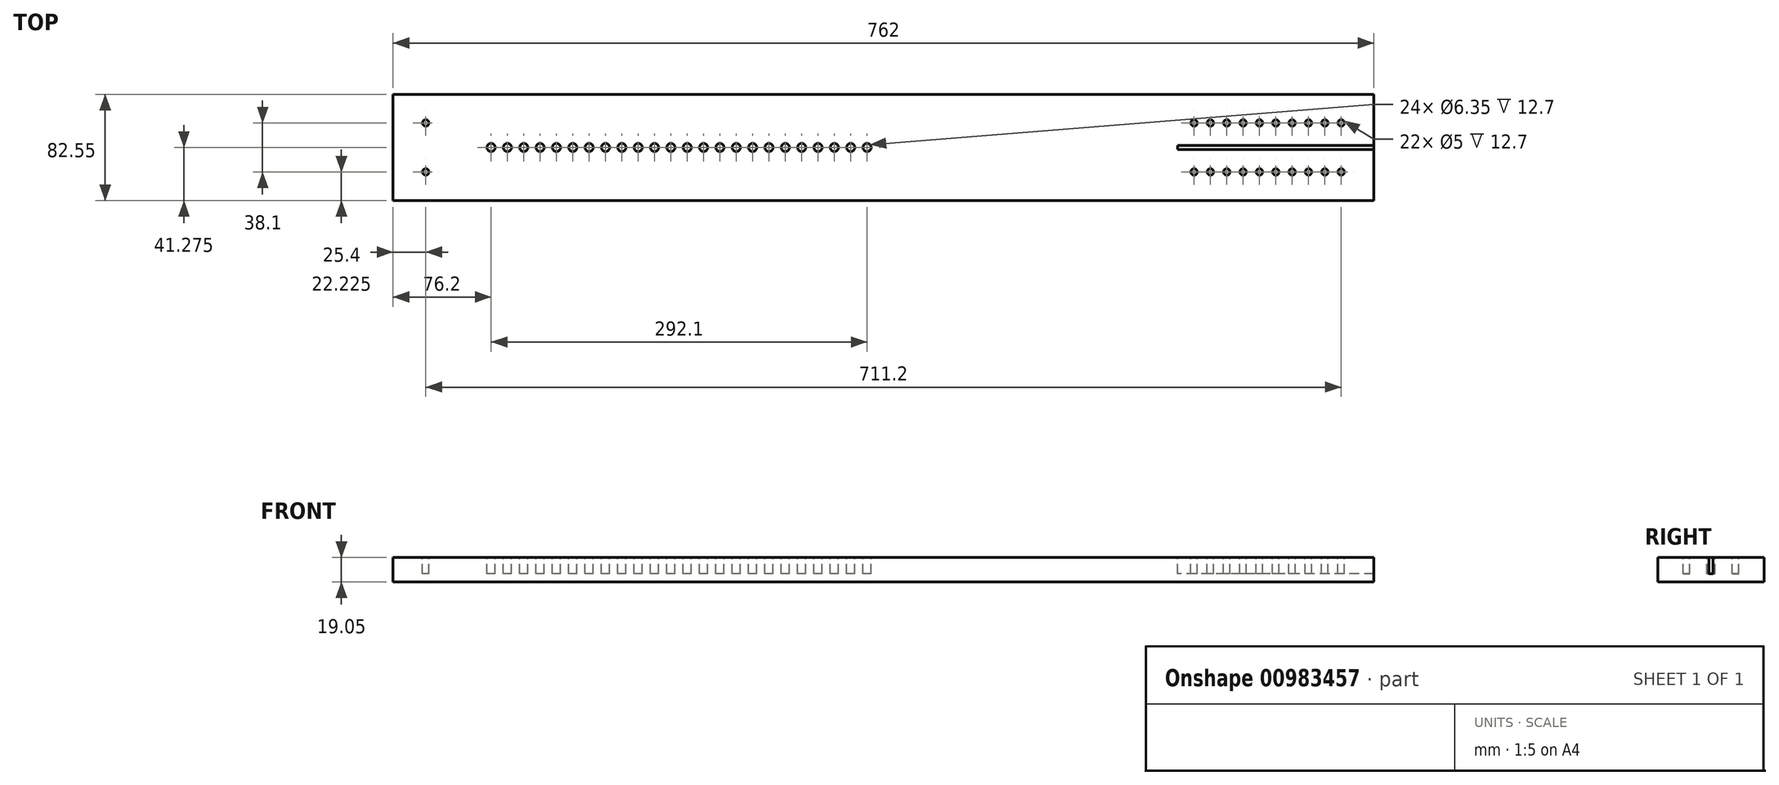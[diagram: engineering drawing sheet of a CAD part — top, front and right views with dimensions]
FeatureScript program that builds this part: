
annotation { "Feature Type Name" : "Feature", "Feature Type Description" : "" }
export const myFeature = defineFeature(function(context is Context, id is Id, definition is map)
    precondition{}
    {
        {
            var Q0;
            Q0=qCreatedBy(makeId("Top.planeOp"),FACE);
            var sketch = newSketch(context, id + "F0", { "sketchPlane" : qUnion([Q0])});
            skLineSegment(sketch, "E0.bottom", {"start": v(0, 0) * mm, "end": v(762, 0) * mm});
            skLineSegment(sketch, "E0.top", {"start": v(0, -82.55) * mm, "end": v(762, -82.55) * mm});
            skLineSegment(sketch, "E0.left", {"start": v(0, 0) * mm, "end": v(0, -82.55) * mm});
            skLineSegment(sketch, "E0.right", {"start": v(762, 0) * mm, "end": v(762, -82.55) * mm});
            skSolve(sketch);
        }
        {
            var Q0;
            Q0 = qSketchRegion(id + "F0", true);
            extrude(context, id + "F1", {"entities" : qUnion([Q0]), "depth" : 19.05 * mm, "offsetDistance" : 25.4 * mm});
        }
        {
            var Q0;
            Q0=makeQuery(id+"F1.opExtrude","CAP_FACE",FACE,{"disambiguationData":[OSD([sQuery(id+"F0.wireOp",EDGE,"E0.bottom"),sQuery(id+"F0.wireOp",EDGE,"E0.top"),sQuery(id+"F0.wireOp",EDGE,"E0.left"),sQuery(id+"F0.wireOp",EDGE,"E0.right")])],"isStart":false});
            var sketch = newSketch(context, id + "F2", { "sketchPlane" : qUnion([Q0])});
            skCircle(sketch, "E1", {"center": v(25.4, -22.23) * mm, "radius": 2.5 * mm});
            skCircle(sketch, "E2", {"center": v(25.4, -60.33) * mm, "radius": 2.5 * mm});
            skCircle(sketch, "E3", {"center": v(76.2, -41.28) * mm, "radius": 3.18 * mm});
            skCircle(sketch, "E4", {"center": v(736.6, -22.23) * mm, "radius": 2.5 * mm});
            skCircle(sketch, "E5", {"center": v(736.6, -60.33) * mm, "radius": 2.5 * mm});
            skLineSegment(sketch, "E6", {"start": v(0, -41.28) * mm, "end": v(762, -41.28) * mm, "construction": true});
            skCircle(sketch, "E7.1.0.0", {"center": v(88.9, -41.28) * mm, "radius": 3.18 * mm});
            skCircle(sketch, "E7.2.0.0", {"center": v(101.6, -41.28) * mm, "radius": 3.18 * mm});
            skCircle(sketch, "E7.3.0.0", {"center": v(114.3, -41.28) * mm, "radius": 3.18 * mm});
            skCircle(sketch, "E7.4.0.0", {"center": v(127, -41.28) * mm, "radius": 3.18 * mm});
            skCircle(sketch, "E7.5.0.0", {"center": v(139.7, -41.28) * mm, "radius": 3.18 * mm});
            skCircle(sketch, "E7.6.0.0", {"center": v(152.4, -41.28) * mm, "radius": 3.18 * mm});
            skCircle(sketch, "E7.7.0.0", {"center": v(165.1, -41.28) * mm, "radius": 3.18 * mm});
            skCircle(sketch, "E7.8.0.0", {"center": v(177.8, -41.28) * mm, "radius": 3.18 * mm});
            skCircle(sketch, "E7.9.0.0", {"center": v(190.5, -41.28) * mm, "radius": 3.18 * mm});
            skCircle(sketch, "E7.10.0.0", {"center": v(203.2, -41.28) * mm, "radius": 3.18 * mm});
            skCircle(sketch, "E7.11.0.0", {"center": v(215.9, -41.28) * mm, "radius": 3.18 * mm});
            skLineSegment(sketch, "E7.direction1", {"start": v(76.2, -41.28) * mm, "end": v(88.9, -41.28) * mm, "construction": true});
            skCircle(sketch, "E8.1.0.0", {"center": v(723.9, -22.23) * mm, "radius": 2.5 * mm});
            skCircle(sketch, "E8.1.0.1", {"center": v(723.9, -60.33) * mm, "radius": 2.5 * mm});
            skCircle(sketch, "E8.2.0.0", {"center": v(711.2, -22.23) * mm, "radius": 2.5 * mm});
            skCircle(sketch, "E8.2.0.1", {"center": v(711.2, -60.33) * mm, "radius": 2.5 * mm});
            skCircle(sketch, "E8.3.0.0", {"center": v(698.5, -22.23) * mm, "radius": 2.5 * mm});
            skCircle(sketch, "E8.3.0.1", {"center": v(698.5, -60.33) * mm, "radius": 2.5 * mm});
            skCircle(sketch, "E8.4.0.0", {"center": v(685.8, -22.23) * mm, "radius": 2.5 * mm});
            skCircle(sketch, "E8.4.0.1", {"center": v(685.8, -60.33) * mm, "radius": 2.5 * mm});
            skCircle(sketch, "E8.5.0.0", {"center": v(673.1, -22.23) * mm, "radius": 2.5 * mm});
            skCircle(sketch, "E8.5.0.1", {"center": v(673.1, -60.33) * mm, "radius": 2.5 * mm});
            skCircle(sketch, "E8.6.0.0", {"center": v(660.4, -22.23) * mm, "radius": 2.5 * mm});
            skCircle(sketch, "E8.6.0.1", {"center": v(660.4, -60.33) * mm, "radius": 2.5 * mm});
            skCircle(sketch, "E8.7.0.0", {"center": v(647.7, -22.23) * mm, "radius": 2.5 * mm});
            skCircle(sketch, "E8.7.0.1", {"center": v(647.7, -60.33) * mm, "radius": 2.5 * mm});
            skCircle(sketch, "E8.8.0.0", {"center": v(635, -22.23) * mm, "radius": 2.5 * mm});
            skCircle(sketch, "E8.8.0.1", {"center": v(635, -60.33) * mm, "radius": 2.5 * mm});
            skLineSegment(sketch, "E8.direction1", {"start": v(736.6, -60.33) * mm, "end": v(723.9, -60.33) * mm, "construction": true});
            skLineSegment(sketch, "E9.bottom", {"start": v(762, -42.86) * mm, "end": v(609.6, -42.86) * mm});
            skLineSegment(sketch, "E9.top", {"start": v(762, -39.69) * mm, "end": v(609.6, -39.69) * mm});
            skLineSegment(sketch, "E9.left", {"start": v(762, -42.86) * mm, "end": v(762, -39.69) * mm});
            skLineSegment(sketch, "E9.right", {"start": v(609.6, -42.86) * mm, "end": v(609.6, -39.69) * mm});
            skCircle(sketch, "E10.0.9.0", {"center": v(622.3, -22.23) * mm, "radius": 2.5 * mm});
            skCircle(sketch, "E10.2.9.0", {"center": v(622.3, -60.33) * mm, "radius": 2.5 * mm});
            skCircle(sketch, "E11.0.12.0", {"center": v(228.6, -41.28) * mm, "radius": 3.18 * mm});
            skCircle(sketch, "E11.0.13.0", {"center": v(241.3, -41.28) * mm, "radius": 3.18 * mm});
            skCircle(sketch, "E11.0.14.0", {"center": v(254, -41.28) * mm, "radius": 3.18 * mm});
            skCircle(sketch, "E11.0.15.0", {"center": v(266.7, -41.28) * mm, "radius": 3.18 * mm});
            skCircle(sketch, "E11.0.16.0", {"center": v(279.4, -41.28) * mm, "radius": 3.18 * mm});
            skCircle(sketch, "E11.0.17.0", {"center": v(292.1, -41.28) * mm, "radius": 3.18 * mm});
            skCircle(sketch, "E11.0.18.0", {"center": v(304.8, -41.28) * mm, "radius": 3.18 * mm});
            skCircle(sketch, "E11.0.19.0", {"center": v(317.5, -41.28) * mm, "radius": 3.18 * mm});
            skCircle(sketch, "E11.0.20.0", {"center": v(330.2, -41.28) * mm, "radius": 3.18 * mm});
            skCircle(sketch, "E11.0.21.0", {"center": v(342.9, -41.28) * mm, "radius": 3.18 * mm});
            skCircle(sketch, "E11.0.22.0", {"center": v(355.6, -41.28) * mm, "radius": 3.18 * mm});
            skCircle(sketch, "E11.0.23.0", {"center": v(368.3, -41.28) * mm, "radius": 3.18 * mm});
            skSolve(sketch);
        }
        {
            var Q0;
            Q0 = qSketchRegion(id + "F2", true);
            extrude(context, id + "F3", {"entities" : qUnion([Q0]), "operationType" : NewBodyOperationType.REMOVE, "oppositeDirection" : true, "depth" : 12.7 * mm, "offsetDistance" : 25.4 * mm});
        }
    });
